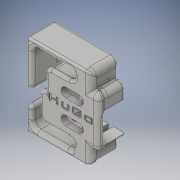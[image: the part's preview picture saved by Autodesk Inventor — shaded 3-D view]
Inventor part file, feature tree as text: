
AUTODESK INVENTOR PART (.ipt)
format: ipt  version: 2016 (Build 200138000, 138)  size: 980,480 bytes
history: native  units: in
note: dims shown in document units (in); Inventor stores cm internally (conversion verified against a paired STEP export)
features: sketch x21, fillet x19, extrude x9, other x3, hole x2, plane x2, thicken_offset x1
ambient origin geometry x8: Origin, YZ Plane, XZ Plane, XY Plane, X Axis, Y Axis, Z Axis, Center Point
bodies: Solid1 (feature_tree)
feature tree (57):
  other  "Hip_rotation_temp.ipt"
  extrude  "Extrusion1"  Depth=0.3937in TaperAngle=0.0deg
  extrude  "Extrusion2"  Depth=0.0787in
  sketch  "Sketch15"  dims[d31=0.0059in d32=0.0059in]
  fillet  "Fillet1"  Radius=0.1969in
  thicken_offset  "Thicken1"
  fillet  "Fillet2"  Radius=0.002in
  fillet  "Fillet3"  Radius=0.1181in
  fillet  "Fillet4"  Radius=0.1181in
  fillet  "Fillet5"  Radius=0.1181in
  fillet  "Fillet6"  Radius=0.1181in
  fillet  "Fillet7"  Radius=0.0354in
  fillet  "Fillet8"  Radius=0.0394in
  fillet  "Fillet9"  Radius=0.0394in
  fillet  "Fillet10"  Radius=0.0591in
  fillet  "Fillet11"  Radius=0.0512in
  fillet  "Fillet12"  Radius=0.1969in
  fillet  "Fillet13"  Radius=0.0787in
  fillet  "Fillet14"  Radius=0.0591in
  extrude  "Extrusion3"  Depth=0.0787in TaperAngle=0.0deg
  fillet  "Fillet15"  Radius=0.1181in
  fillet  "Fillet17"  Radius=0.0394in
  fillet  "Fillet18"  Radius=0.0787in
  extrude  "Extrusion4"  Depth=0.1575in TaperAngle=0.0deg
  extrude  "Extrusion5"  Depth=0.0059in
  hole  "Hole1"  [1 undecoded]
  extrude  "Extrusion6"  Depth=0.2953in
  extrude  "Extrusion7"  Depth=0.2362in
  extrude  "Extrusion8"  Depth=0.0394in
  hole  "Hole2"  [1 undecoded]
  fillet  "Fillet19"  Radius=0.3051in
  extrude  "Extrusion9"  Depth=0.0965in
  fillet  "Fillet20"  Radius=0.0965in
  other  "Solid1::Hip_rotation_temp.ipt"
  other  "TaggingFeature1"
  sketch  "Sketch1"  dims[d0=0.3937in d1=0.4724in d2=0.0in]
  sketch  "Sketch12"  dims[d3=0.9843in d4=0.0in d5=0.0787in d6=0.1969in d7=0.002in d8=0.0013in d9=0.1181in d10=0.1181in d11=0.1181in d12=0.1181in d13=0.0354in d14=0.0394in d15=0.0394in d16=0.0591in d17=0.0512in d18=0.1969in d19=0.0787in d20=0.0591in]
  sketch  "Sketch14"  dims[d28=0.2835in d29=0.1575in d30=0.0in]
  sketch  "Sketch17"  dims[d36=0.2953in d38=0.2953in]
  sketch  "Sketch18"  dims[d39=0.2362in d40=0.2362in]
  sketch  "Sketch20"  dims[d41=0.0591in d42=0.2362in d43=0.1181in d44=0.0394in d45=90.0deg d46=0.315in d47=0.8108in d48=0.1969in d49=0.1969in d50=0.2756in d51=0.2756in]
  sketch  "Sketch21"  dims[d52=0.3051in d53=0.3051in d54=0.3051in]
  sketch  "Sketch22"  dims[d55=0.315in d56=0.0965in d57=0.0965in]
  sketch  "Sketch25"  dims[d60=0.0197in d61=0.0in]
  sketch  "Sketch26"  dims[d62=0.5197in]
  sketch  "Sketch27"  dims[d63=0.6043in]
  plane  "Work Plane1"
  plane  "Work Plane2"
  sketch  "Sketch13"  dims[d21=0.0354in d22=1.4961in d23=0.0in d24=0.1181in d26=0.0394in d27=0.0787in]
  sketch  "Sketch16"  dims[d33=0.4724in d34=0.0in d35=0.2953in]
  sketch  "Sketch24"  dims[d58=0.3937in d59=0.0in]
  sketch  "Sketch28"  dims[d64=0.6043in]
  sketch  "Sketch29"  dims[d65=0.5257in d66=0.0in]
  sketch  "Sketch31"  dims[d67=0.2756in]
  sketch  "Sketch32"  dims[d70=0.0591in d71=0.2362in d72=0.1575in d73=0.0787in d74=90.0deg d75=0.315in d76=0.8108in]
  sketch  "Sketch34"  dims[d77=0.0748in]
  sketch  "Sketch35"  dims[d78=0.2835in d79=0.9409in d80=0.5039in d81=0.0in d82=0.1181in d83=0.0in d84=0.1575in d85=0.0748in]
note: 2 required parameter values undecoded (feature->parameter linkage not recoverable at this tier; creation-order binding heuristic only, values carry confidence <= 0.55)
